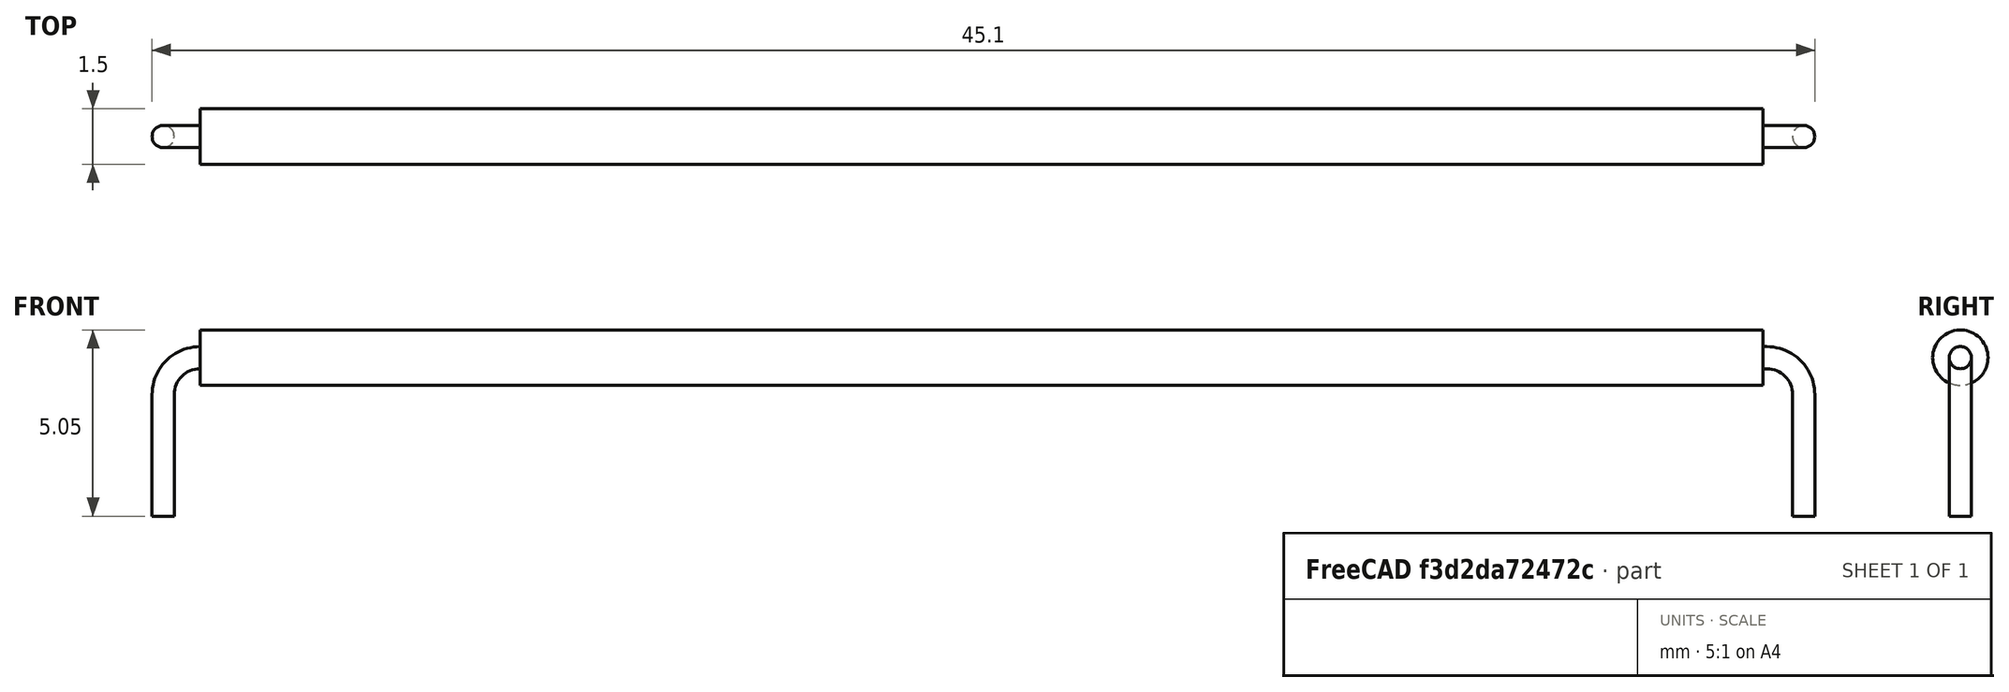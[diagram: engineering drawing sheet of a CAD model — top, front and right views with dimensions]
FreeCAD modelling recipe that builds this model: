
FCSTD DOCUMENT  (FreeCAD 0.21R33771 (Git))
Label: Jumper_Base_forTweaking
License: All rights reserved
LicenseURL: http://en.wikipedia.org/wiki/All_rights_reserved
objects: TechDraw::DrawViewDimension×4, Sketcher::SketchObject×3, TechDraw::DrawProjGroupItem×3, PartDesign::Plane×2, PartDesign::AdditivePipe×1, PartDesign::Pad×1, PartDesign::Body×1, App::Part×1, TechDraw::DrawSVGTemplate×1, TechDraw::DrawProjGroup×1, TechDraw::DrawPage×1
note: 10 computed .brp shape members not serialized (recipe doc carries the construction recipe); baked Part::Feature solids carry a one-line shape summary decoded from their .brp

FEATURE [PartDesign::Plane] DatumPlane002  label="DatumPlane_insulEdge"
  AttachmentOffset = pos=(0,0,1) rot=(0,0,1;0rad)
  Length = 60
  MapMode = 5
  Placement = pos=(1,-2e-16,2e-16) rot=(0.57735,0.57735,0.57735;2.0944rad)
  ResizeMode = 0
  Support = -> [YZ_Plane001]
  Width = 60
FEATURE [PartDesign::Plane] DatumPlane
  AttachmentOffset = pos=(0,0,-3) rot=(0,0,1;0rad)
  Length = 81.6152
  MapMode = 5
  Placement = pos=(0,0,-3) rot=(0,0,1;0rad)
  ResizeMode = 0
  Support = -> [XY_Plane001]
  Width = 61.8152
FEATURE [Sketcher::SketchObject] Sketch  label="Sketch_Path"
  FullyConstrained = true
  MapMode = 5
  Placement = pos=(0,0,0) rot=(1,0,0;1.5708rad)
  Support = -> [XZ_Plane001]
  sketch-geometry (5):
    g0: LineSegment StartX=0 StartY=-3 StartZ=0 EndX=0 EndY=0.3 EndZ=0
    g1: LineSegment StartX=1 StartY=1.3 StartZ=0 EndX=43.5 EndY=1.3 EndZ=0
    g2: LineSegment StartX=44.5 StartY=0.3 StartZ=0 EndX=44.5 EndY=-3 EndZ=0
    g3: ArcOfCircle CenterX=1 CenterY=0.3 CenterZ=0 NormalX=0 NormalY=0 NormalZ=1 AngleXU=0 Radius=1 StartAngle=1.5708 EndAngle=3.14159
    g4: ArcOfCircle CenterX=43.5 CenterY=0.3 CenterZ=0 NormalX=0 NormalY=0 NormalZ=1 AngleXU=0 Radius=1 StartAngle=0 EndAngle=1.5708
  constraints (14):
    c: PointOnObject(g0,g-2)
    c: Horizontal(g1)
    c: Vertical(g2)
    c: DistanceX(g-1,g2) = 44.5
    c: DistanceY(g0,g-1) = 3
    c: DistanceY(g2,g-1) = 3
    c: Tangent(g0,g3) = 1.5708
    c: Tangent(g1,g3) = 1.5708
    c: Tangent(g1,g4) = 1.5708
    c: Tangent(g2,g4) = 1.5708
    c: Radius(g3) = 1
    c: Radius(g4) = 1
    c: Vertical(g0)
    c: DistanceY(g-1,g1) = 1.3
FEATURE [Sketcher::SketchObject] Sketch001  label="Sketch_Section"
  FullyConstrained = true
  MapMode = 5
  Placement = pos=(0,0,-3) rot=(0,0,1;0rad)
  Support = -> [DatumPlane]
  sketch-geometry (1):
    g0: Circle CenterX=0 CenterY=0 CenterZ=0 NormalX=0 NormalY=0 NormalZ=1 AngleXU=0 Radius=0.3
  constraints (2):
    c: Coincident(g0,g-1)
    c: Diameter(g0) = 0.6
FEATURE [PartDesign::AdditivePipe] AdditivePipe  label="AdditivePipe-Wire"
  AuxilleryCurvelinear = true
  AuxillerySpineTangent = false
  Binormal = (0,0,0)
  Mode = 0
  Placement = pos=(0,0,-3) rot=(0,0,1;0rad)
  Profile = -> Sketch001
  Spine = -> Sketch [Edge1,Edge2,Edge3,Edge4,Edge5]
  SpineTangent = false
  Transformation = 0
  Transition = 0
FEATURE [Sketcher::SketchObject] Sketch002
  ExternalGeometry = -> [AdditivePipe]
  FullyConstrained = true
  MapMode = 5
  Placement = pos=(1,-2e-16,2e-16) rot=(0.57735,0.57735,0.57735;2.0944rad)
  Support = -> [DatumPlane002]
  sketch-geometry (1):
    g0: Circle CenterX=0 CenterY=1.3 CenterZ=0 NormalX=0 NormalY=0 NormalZ=1 AngleXU=0 Radius=0.75
  constraints (2):
    c: Coincident(g0,g-3)
    c: Diameter(g0) = 1.5
FEATURE [PartDesign::Pad] Pad  label="Pad_Insulation"
  BaseFeature = -> AdditivePipe
  Direction = (1,-1e-16,1e-16)
  Length = 42.4
  Length2 = 10
  Placement = pos=(0,0,-3) rot=(0,0,1;0rad)
  Profile = -> Sketch002
  ReferenceAxis = -> Sketch002 [N_Axis]
  Type = 0
FEATURE [PartDesign::Body] Body  label="Body_JumperBase"
  Group = -> [DatumPlane002,DatumPlane,Sketch,Sketch001,AdditivePipe,Sketch002,Pad]
  Origin = -> Origin001
  Tip = -> Pad
FEATURE [App::Part] Part
  Group = -> [Body]
  Origin = -> Origin
FEATURE [TechDraw::DrawSVGTemplate] Template
  EditableTexts = myDrawingName=Jumper_Baseline; myEditableField=Drawing Number; myFieldName=Date; myScale=Scale; mySheet=Sheet
  Height = 215.9
  Orientation = 1
  Width = 279.4
FEATURE [TechDraw::DrawProjGroupItem] ProjItem  label="Front"
  CoarseView = false
  Direction = (0,-1,0)
  Focus = 100
  HardHidden = true
  IsoCount = 0
  IsoHidden = false
  IsoVisible = false
  LockPosition = true
  Perspective = false
  Rotation = 0
  RotationVector = (1,0,0)
  Scale = 3
  ScaleType = 2
  ScrubCount = 0
  SeamHidden = false
  SeamVisible = true
  SmoothHidden = false
  SmoothVisible = true
  Source = -> [Pad]
  Type = 0
  X = 0
  XDirection = (1,0,0)
  Y = 0
FEATURE [TechDraw::DrawProjGroupItem] ProjItem001  label="Left"
  CoarseView = false
  Direction = (-1,-1e-16,0)
  Focus = 100
  HardHidden = true
  IsoCount = 0
  IsoHidden = false
  IsoVisible = false
  LockPosition = false
  Perspective = false
  Rotation = 0
  RotationVector = (1,0,0)
  ScaleType = 2
  ScrubCount = 0
  SeamHidden = false
  SeamVisible = true
  SmoothHidden = false
  SmoothVisible = true
  Source = -> [Pad]
  Type = 1
  X = 84.9
  XDirection = (1e-16,-1,0)
  Y = 0
FEATURE [TechDraw::DrawProjGroupItem] ProjItem002  label="FrontTopRight"
  CoarseView = false
  Direction = (0.57735,-0.57735,0.57735)
  Focus = 100
  HardHidden = true
  IsoCount = 0
  IsoHidden = false
  IsoVisible = false
  LockPosition = true
  Perspective = false
  Rotation = 0
  RotationVector = (1,0,0)
  ScaleType = 2
  ScrubCount = 0
  SeamHidden = false
  SeamVisible = true
  SmoothHidden = false
  SmoothVisible = true
  Source = -> [Pad]
  Type = 7
  X = -88.3379
  XDirection = (0.707107,0.707107,0)
  Y = -40.9409
FEATURE [TechDraw::DrawProjGroup] ProjGroup
  Anchor = -> ProjItem
  AutoDistribute = true
  LockPosition = false
  ProjectionType = 0
  Rotation = 0
  Scale = 3
  ScaleType = 2
  Source = -> [Pad]
  Views = -> [ProjItem,ProjItem001,ProjItem002]
  X = 159.623
  Y = 151.819
  spacingX = 15
  spacingY = 15
FEATURE [TechDraw::DrawViewDimension] Dimension
  AngleOverride = false
  Arbitrary = false
  ArbitraryTolerances = false
  EqualTolerance = true
  ExtensionAngle = 0
  FormatSpec = %.2f
  FormatSpecOverTolerance = %+.2f
  FormatSpecUnderTolerance = %+.2f
  Inverted = false
  LineAngle = 0
  LockPosition = false
  MeasureType = 1
  OverTolerance = 0
  References2D = -> [ProjItem]
  Rotation = 0
  ScaleType = 2
  TheoreticalExact = false
  Type = 1
  UnderTolerance = 0
  X = 0.588358
  Y = -15.3427
FEATURE [TechDraw::DrawViewDimension] Dimension001
  AngleOverride = false
  Arbitrary = false
  ArbitraryTolerances = false
  EqualTolerance = true
  ExtensionAngle = 0
  FormatSpec = ⌀%.2f
  FormatSpecOverTolerance = %+.2f
  FormatSpecUnderTolerance = %+.2f
  Inverted = false
  LineAngle = 0
  LockPosition = false
  MeasureType = 1
  OverTolerance = 0
  References2D = -> [ProjItem001]
  Rotation = 0
  ScaleType = 2
  TheoreticalExact = false
  Type = 5
  UnderTolerance = 0
  X = 14.1264
  Y = 17.5599
FEATURE [TechDraw::DrawViewDimension] Dimension002
  AngleOverride = false
  Arbitrary = false
  ArbitraryTolerances = false
  EqualTolerance = true
  ExtensionAngle = 0
  FormatSpec = ⌀%.2f
  FormatSpecOverTolerance = %+.2f
  FormatSpecUnderTolerance = %+.2f
  Inverted = false
  LineAngle = 0
  LockPosition = false
  MeasureType = 1
  OverTolerance = 0
  References2D = -> [ProjItem001]
  Rotation = 0
  ScaleType = 2
  TheoreticalExact = false
  Type = 5
  UnderTolerance = 0
  X = -7.74992
  Y = 21.2878
FEATURE [TechDraw::DrawViewDimension] Dimension003
  AngleOverride = false
  Arbitrary = false
  ArbitraryTolerances = false
  EqualTolerance = true
  ExtensionAngle = 0
  FormatSpec = %.2f
  FormatSpecOverTolerance = %+.2f
  FormatSpecUnderTolerance = %+.2f
  Inverted = false
  LineAngle = 0
  LockPosition = false
  MeasureType = 1
  OverTolerance = 0
  References2D = -> [ProjItem001]
  Rotation = 0
  ScaleType = 2
  TheoreticalExact = false
  Type = 2
  UnderTolerance = 0
  X = -16.3422
  Y = 0.373555
FEATURE [TechDraw::DrawPage] Page
  KeepUpdated = true
  NextBalloonIndex = 1
  ProjectionType = 0
  Template = -> Template
  Views = -> [ProjGroup,Dimension,Dimension001,Dimension002,Dimension003]
